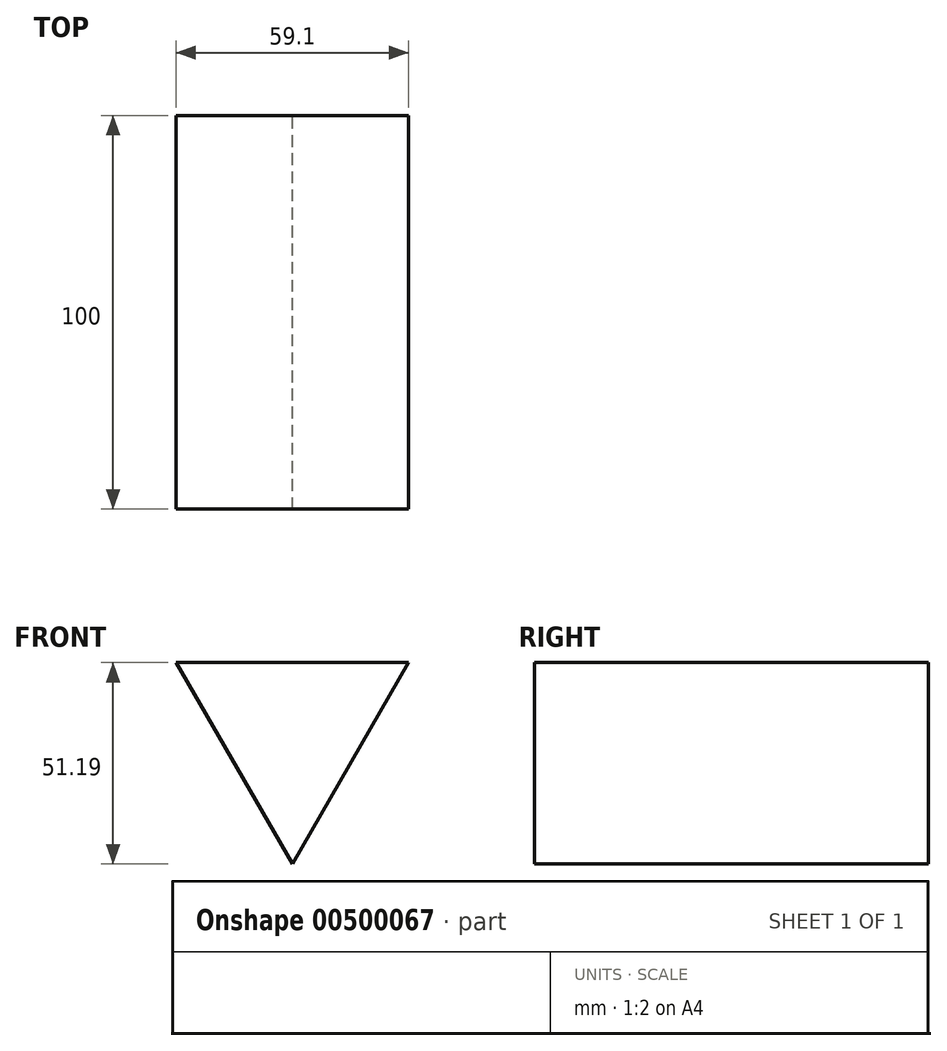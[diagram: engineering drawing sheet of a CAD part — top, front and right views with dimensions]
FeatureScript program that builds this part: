
annotation { "Feature Type Name" : "Feature", "Feature Type Description" : "" }
export const myFeature = defineFeature(function(context is Context, id is Id, definition is map)
    precondition{}
    {
        {
            var Q0;
            Q0=qCreatedBy(makeId("Front.planeOp"),FACE);
            var sketch = newSketch(context, id + "F0", { "sketchPlane" : qUnion([Q0])});
            skCircle(sketch, "E0.cCircle", {"center": v(0, 0) * mm, "radius": 34.13 * mm, "construction": true});
            skLineSegment(sketch, "E0.0", {"start": v(0, -34.13) * mm, "end": v(-29.55, 17.06) * mm});
            skLineSegment(sketch, "E0.1", {"start": v(-29.55, 17.06) * mm, "end": v(29.55, 17.06) * mm});
            skLineSegment(sketch, "E0.2", {"start": v(29.55, 17.06) * mm, "end": v(0, -34.13) * mm});
            skSolve(sketch);
        }
        {
            var Q0;
            Q0=makeQuery(id+"F0.imprint","IMPRINT",FACE,{"disambiguationData":[TD([[makeQuery(id+"F0.imprint","IMPRINT",EDGE,{"derivedFrom":sQuery(id+"F0.wireOp",EDGE,"E0.0")}),-1.0]])]});
            extrude(context, id + "F1", {"entities" : qUnion([Q0]), "endBound" : BoundingType.SYMMETRIC, "depth" : 100 * mm});
        }
    });
